# Revit family: 754000001_Ducha Antivandalica Regadera Tubular
name_source: partatom
category: Plumbing Fixtures
units: mm (PartAtom-declared; Revit-internal decimal feet)

## family parameters
Always vertical = Yes
Cut with Voids When Loaded = No
Host = Wall
OmniClass Number = 23.31.11.00
OmniClass Title = Faucets
Part Type = Normal
Room Calculation Point = No
Round Connector Dimension = Use Diameter
Shared = No

## types (1)
- 754000001_Ducha Antivandalica Regadera Tubular
    Alto = 84 mm
    Alto 2 = 74 mm  [stored 0.242782 ft]
    Ancho = 55 mm  [stored 0.180446 ft]
    Ancho 2 = 74 mm  [stored 0.242782 ft]
    Capacidad de flujo = 6,6 L/min - 3,3 L/Descarga A 80 Psi
    Ciclo de vida de la unidad de cierre = 150,000 ciclos.
    Creado por = BIMBAU
    Default Elevation = 0 mm  [stored 0 ft]
    Description = Las duchas Corona son el aliado perfecto para las necesidades de las
instituciones de alto tráfico, están diseñadas para un óptimo
funcionamiento y durabilidad debido a sus características antivandálicas
    Diametro de Tubería para la Instalación = 1/2  NPT.
    Fecha de creación = 16/03/2021
    Garantía = 3 Años
    Manufacturer = Corona
    Material = Corona_Aluminio
    Material 2 = Corona_Cobre
    Model = Ducha antivandalica con regadera tubular
    Peso Bruto aprox = 880gr. / 1,94Lb
    Peso Neto aprox = 760gr. / 1,68Lb.
    Presion maxima = 80 Psi elástica.
    Presion minima = 20 Psi elástica.
    Profundidad = 198 mm  [stored 0.649606 ft]
    Profundidad 2 = 90 mm
    Referencia = 754000001

note: [stored X ft] marks values corroborated as IEEE doubles in the binary element streams (Revit-internal decimal feet)

## geometry (parser evidence)
native form markers: Sweep x6
no freeform markers — native parametric forms only
